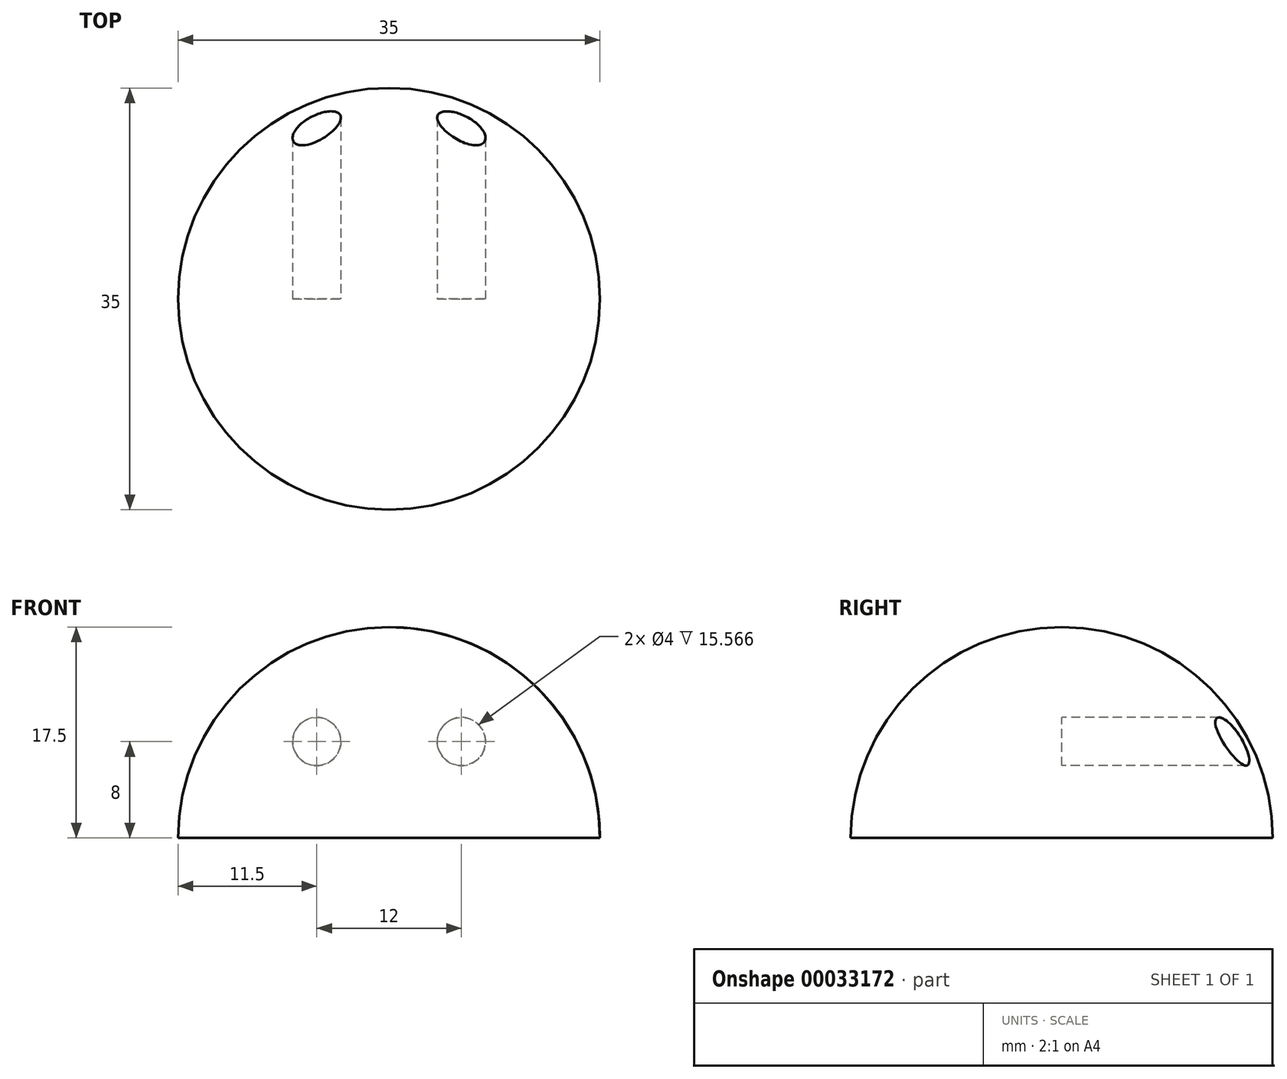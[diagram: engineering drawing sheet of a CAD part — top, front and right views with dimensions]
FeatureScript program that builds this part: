
annotation { "Feature Type Name" : "Feature", "Feature Type Description" : "" }
export const myFeature = defineFeature(function(context is Context, id is Id, definition is map)
    precondition{}
    {
        {
            var Q0;
            Q0=qCreatedBy(makeId("Front.planeOp"),FACE);
            var sketch = newSketch(context, id + "F0", { "sketchPlane" : qUnion([Q0])});
            skArc(sketch, "E0", {"start": v(17.5, 0) * mm, "mid": v(12.37, 12.37) * mm, "end": v(0, 17.5) * mm});
            skLineSegment(sketch, "E1", {"start": v(0, 0) * mm, "end": v(0, 17.5) * mm});
            skLineSegment(sketch, "E2", {"start": v(0, 0) * mm, "end": v(17.5, 0) * mm});
            skSolve(sketch);
        }
        {
            var Q0;
            Q0 = qSketchRegion(id + "F0", true);
            var Q1;
            Q1=sQuery(id+"F0.wireOp",EDGE,"E1");
            revolve(context, id + "F1", {"entities" : qUnion([Q0]), "axis" : qUnion([Q1]), "revolveType" : RevolveType.FULL});
        }
        {
            var Q0;
            Q0=qCreatedBy(makeId("Front.planeOp"),FACE);
            var sketch = newSketch(context, id + "F2", { "sketchPlane" : qUnion([Q0])});
            skCircle(sketch, "E3", {"center": v(-6, 8) * mm, "radius": 2 * mm});
            skCircle(sketch, "E4.MirrorC", {"center": v(6, 8) * mm, "radius": 2 * mm});
            skSolve(sketch);
        }
        {
            var Q0;
            Q0 = qSketchRegion(id + "F2", true);
            extrude(context, id + "F3", {"entities" : qUnion([Q0]), "operationType" : NewBodyOperationType.REMOVE, "oppositeDirection" : true, "depth" : 25 * mm});
        }
    });
